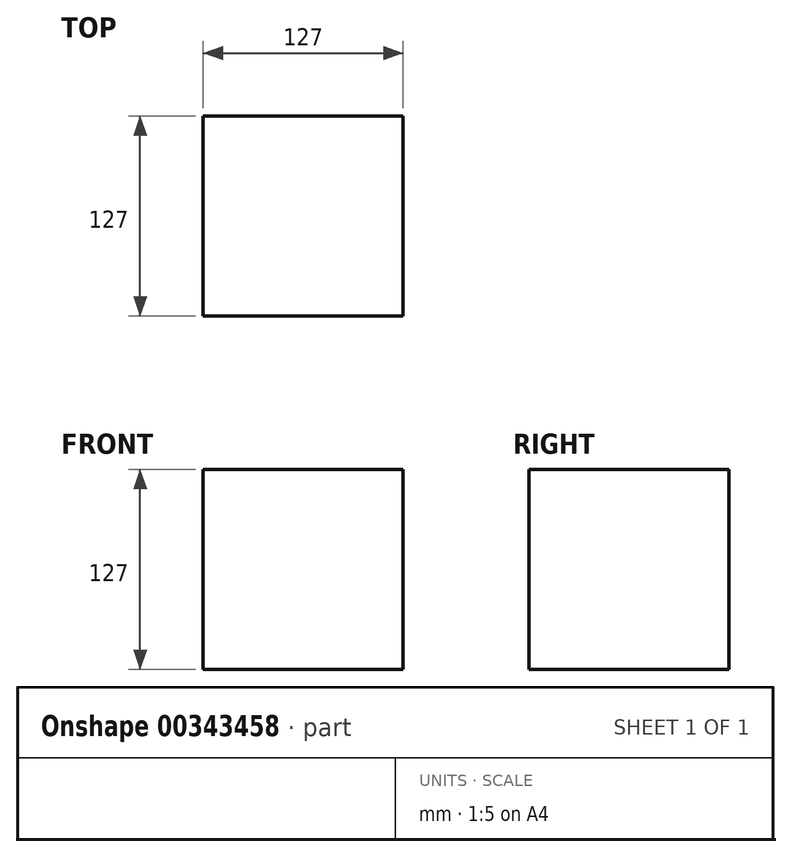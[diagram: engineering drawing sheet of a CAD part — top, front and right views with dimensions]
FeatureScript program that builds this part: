
annotation { "Feature Type Name" : "Feature", "Feature Type Description" : "" }
export const myFeature = defineFeature(function(context is Context, id is Id, definition is map)
    precondition{}
    {
        {
            var Q0;
            Q0=qCreatedBy(makeId("Front.planeOp"),FACE);
            var sketch = newSketch(context, id + "F0", { "sketchPlane" : qUnion([Q0])});
            skLineSegment(sketch, "E0.bottom", {"start": v(-58.42, 83.5) * mm, "end": v(68.58, 83.5) * mm});
            skLineSegment(sketch, "E0.top", {"start": v(-58.42, -43.5) * mm, "end": v(68.58, -43.5) * mm});
            skLineSegment(sketch, "E0.left", {"start": v(-58.42, 83.5) * mm, "end": v(-58.42, -43.5) * mm});
            skLineSegment(sketch, "E0.right", {"start": v(68.58, 83.5) * mm, "end": v(68.58, -43.5) * mm});
            skSolve(sketch);
        }
        {
            var Q0;
            Q0=makeQuery(id+"F0.imprint","IMPRINT",FACE,{"disambiguationData":[TD([[makeQuery(id+"F0.imprint","IMPRINT",EDGE,{"derivedFrom":sQuery(id+"F0.wireOp",EDGE,"E0.bottom")}),-1.0]])]});
            extrude(context, id + "F1", {"entities" : qUnion([Q0]), "depth" : 127 * mm});
        }
    });
